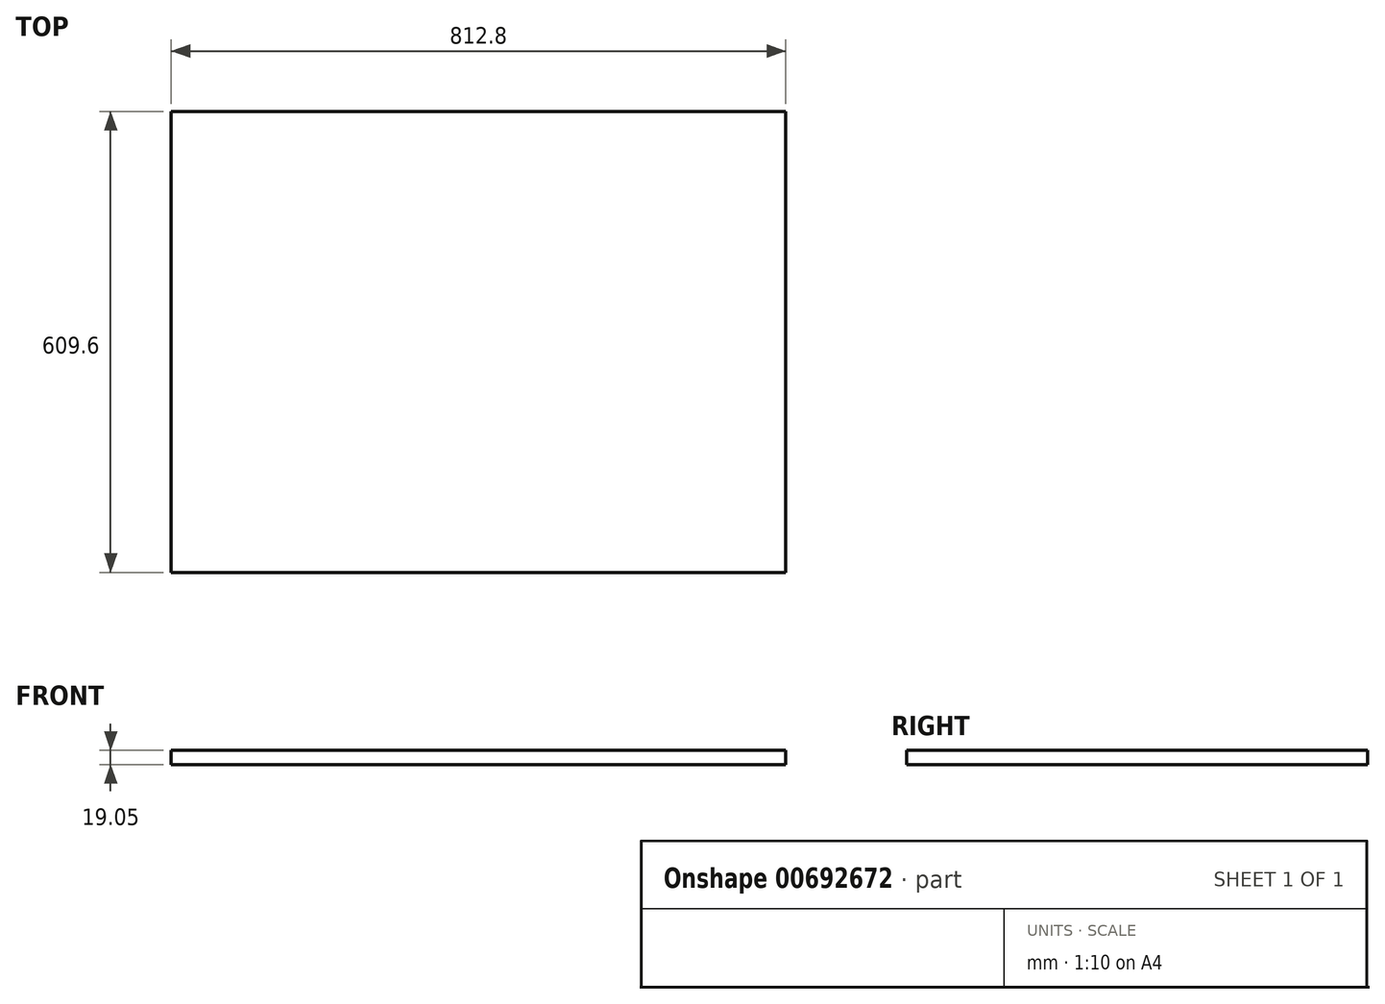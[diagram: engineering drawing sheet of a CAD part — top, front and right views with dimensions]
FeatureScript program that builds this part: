
annotation { "Feature Type Name" : "Feature", "Feature Type Description" : "" }
export const myFeature = defineFeature(function(context is Context, id is Id, definition is map)
    precondition{}
    {
        {
            var Q0;
            Q0=qCreatedBy(makeId("Top.planeOp"),FACE);
            var sketch = newSketch(context, id + "F0", { "sketchPlane" : qUnion([Q0])});
            skLineSegment(sketch, "E0.bottom", {"start": v(-246.1, 380.33) * mm, "end": v(566.7, 380.33) * mm});
            skLineSegment(sketch, "E0.top", {"start": v(-246.1, -229.27) * mm, "end": v(566.7, -229.27) * mm});
            skLineSegment(sketch, "E0.left", {"start": v(-246.1, 380.33) * mm, "end": v(-246.1, -229.27) * mm});
            skLineSegment(sketch, "E0.right", {"start": v(566.7, 380.33) * mm, "end": v(566.7, -229.27) * mm});
            skSolve(sketch);
        }
        {
            var Q0;
            Q0=makeQuery(id+"F0.imprint","IMPRINT",FACE,{"disambiguationData":[TD([[makeQuery(id+"F0.imprint","IMPRINT",EDGE,{"derivedFrom":sQuery(id+"F0.wireOp",EDGE,"E0.bottom")}),-1.0]])]});
            extrude(context, id + "F1", {"entities" : qUnion([Q0]), "oppositeDirection" : true, "depth" : 19.05 * mm, "offsetDistance" : 25.4 * mm});
        }
    });
